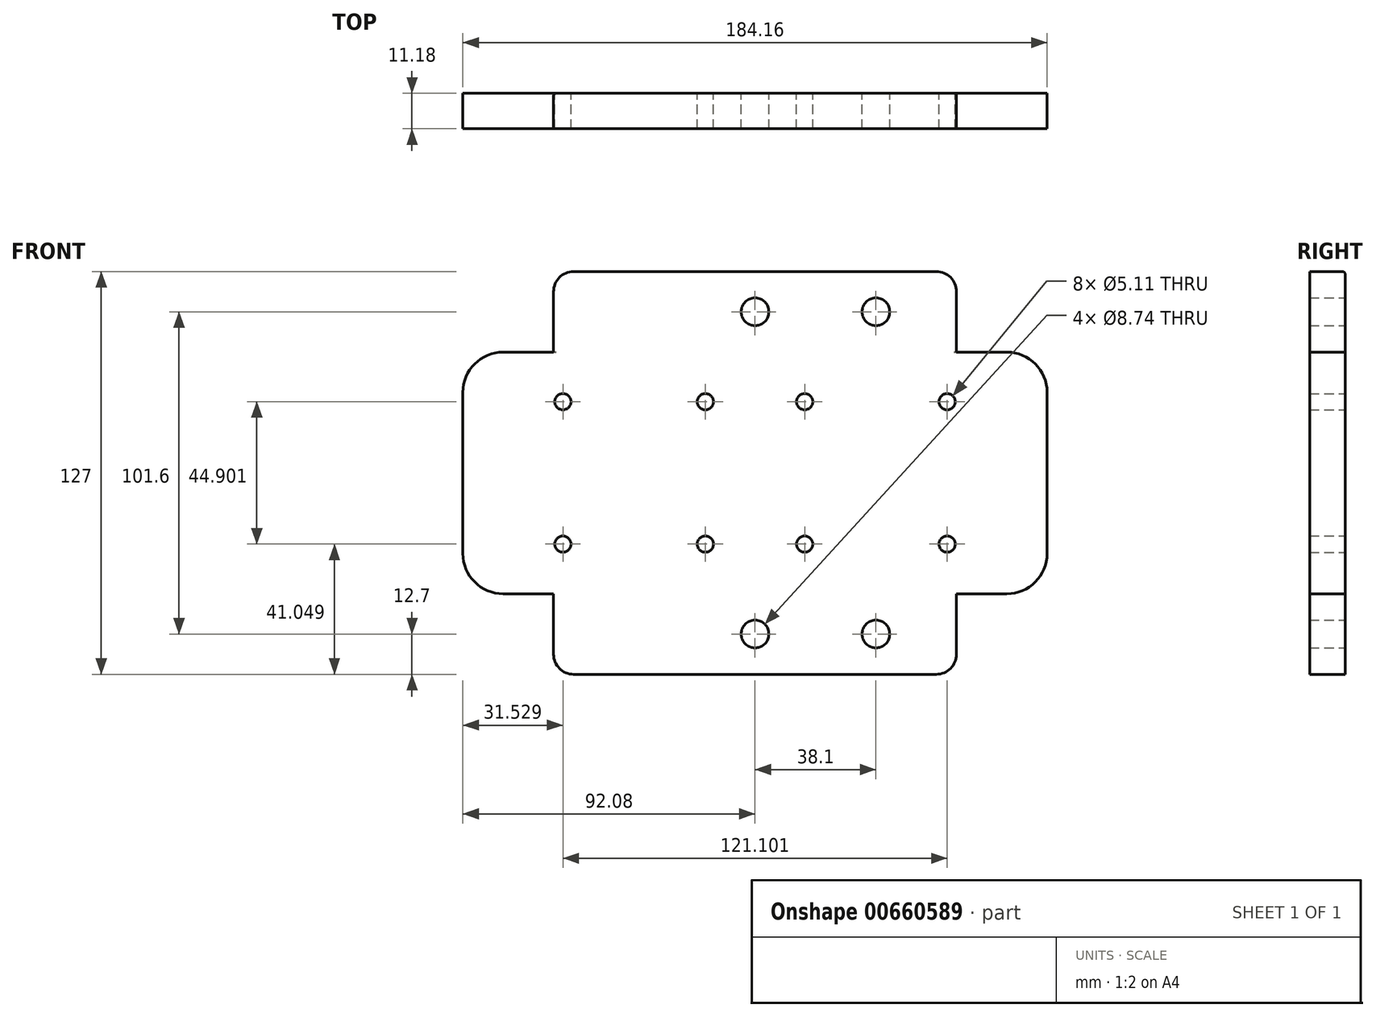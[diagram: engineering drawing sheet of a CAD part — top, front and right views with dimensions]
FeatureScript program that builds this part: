
annotation { "Feature Type Name" : "Feature", "Feature Type Description" : "" }
export const myFeature = defineFeature(function(context is Context, id is Id, definition is map)
    precondition{}
    {
        {
            var Q0;
            Q0=qCreatedBy(makeId("Front.planeOp"),FACE);
            var sketch = newSketch(context, id + "F0", { "sketchPlane" : qUnion([Q0])});
            skLineSegment(sketch, "E0.bottom", {"start": v(92.07, 38.1) * mm, "end": v(-92.08, 38.1) * mm});
            skLineSegment(sketch, "E0.top", {"start": v(92.08, -38.1) * mm, "end": v(-92.08, -38.1) * mm});
            skLineSegment(sketch, "E0.left", {"start": v(92.07, 38.1) * mm, "end": v(92.08, -38.1) * mm});
            skLineSegment(sketch, "E0.right", {"start": v(-92.08, 38.1) * mm, "end": v(-92.08, -38.1) * mm});
            skPoint(sketch, "E0.middle", {"position": v(0, 0) * mm});
            skPoint(sketch, "E1.visualSharp", {"position": v(-92.08, 38.1) * mm});
            skPoint(sketch, "E2.visualSharp", {"position": v(92.07, 38.1) * mm});
            skPoint(sketch, "E3.visualSharp", {"position": v(92.08, -38.1) * mm});
            skPoint(sketch, "E4.visualSharp", {"position": v(-92.08, -38.1) * mm});
            skSolve(sketch);
        }
        {
            var Q0;
            Q0 = qSketchRegion(id + "F0", true);
            extrude(context, id + "F1", {"entities" : qUnion([Q0]), "depth" : 11.18 * mm, "offsetDistance" : 25.4 * mm});
        }
        {
            var Q0;
            Q0=makeQuery(id+"F1.opExtrude","SWEPT_EDGE",EDGE,{"disambiguationData":[OSD([sQuery(id+"F0.wireOp",EDGE,"E0.bottom"),sQuery(id+"F0.wireOp",EDGE,"E0.left")])]});
            var Q1;
            Q1=makeQuery(id+"F1.opExtrude","SWEPT_EDGE",EDGE,{"disambiguationData":[OSD([sQuery(id+"F0.wireOp",EDGE,"E0.top"),sQuery(id+"F0.wireOp",EDGE,"E0.left")])]});
            var Q2;
            Q2=makeQuery(id+"F1.opExtrude","SWEPT_EDGE",EDGE,{"disambiguationData":[OSD([sQuery(id+"F0.wireOp",EDGE,"E0.top"),sQuery(id+"F0.wireOp",EDGE,"E0.right")])]});
            var Q3;
            Q3=makeQuery(id+"F1.opExtrude","SWEPT_EDGE",EDGE,{"disambiguationData":[OSD([sQuery(id+"F0.wireOp",EDGE,"E0.bottom"),sQuery(id+"F0.wireOp",EDGE,"E0.right")])]});
            fillet(context, id + "F2", {"entities" : qUnion([Q0, Q1, Q2, Q3]), "radius" : 12.7 * mm, "tangentPropagation" : true, "allowEdgeOverflow" : false});
        }
        {
            var Q0;
            Q0=qCreatedBy(makeId("Front.planeOp"),FACE);
            var sketch = newSketch(context, id + "F3", { "sketchPlane" : qUnion([Q0])});
            skLineSegment(sketch, "E5.bottom", {"start": v(63.5, 38.1) * mm, "end": v(-63.5, 38.1) * mm});
            skLineSegment(sketch, "E5.top", {"start": v(63.5, 63.5) * mm, "end": v(-63.5, 63.5) * mm});
            skLineSegment(sketch, "E5.left", {"start": v(63.5, 38.1) * mm, "end": v(63.5, 63.5) * mm});
            skLineSegment(sketch, "E5.right", {"start": v(-63.5, 38.1) * mm, "end": v(-63.5, 63.5) * mm});
            skLineSegment(sketch, "E6.MirrorCS", {"start": v(63.5, -38.1) * mm, "end": v(63.5, -63.5) * mm});
            skLineSegment(sketch, "E7.MirrorCS", {"start": v(63.5, -38.1) * mm, "end": v(-63.5, -38.1) * mm});
            skLineSegment(sketch, "E8.MirrorCS", {"start": v(63.5, -63.5) * mm, "end": v(-63.5, -63.5) * mm});
            skLineSegment(sketch, "E9.MirrorCS", {"start": v(-63.5, -38.1) * mm, "end": v(-63.5, -63.5) * mm});
            skSolve(sketch);
        }
        {
            var Q0;
            Q0 = qSketchRegion(id + "F3", true);
            var Q1;
            Q1=makeQuery(id+"F00pBhFej4blYbs_1.boolean.opBoolean","MERGE",FACE,{"derivedFrom":[makeQuery(id+"F1.opExtrude","CAP_FACE",FACE,{"disambiguationData":[OSD([sQuery(id+"F0.wireOp",EDGE,"E0.bottom"),sQuery(id+"F0.wireOp",EDGE,"E0.top"),sQuery(id+"F0.wireOp",EDGE,"E0.left"),sQuery(id+"F0.wireOp",EDGE,"E0.right")])],"isStart":false}),makeQuery(id+"F00pBhFej4blYbs_1.opExtrude","SWEPT_FACE",FACE,{"disambiguationData":[OSD([sQuery(id+"FrYmvnTRkbLSalc_1.wireOp",EDGE,"83ce238e-0b4e-4dba-95ea-3f2d73f66f50.0")])]})]});
            extrude(context, id + "F4", {"entities" : qUnion([Q0]), "operationType" : NewBodyOperationType.ADD, "depth" : 11.18 * mm, "endBoundEntityFace" : qUnion([Q1]), "offsetDistance" : 25.4 * mm});
        }
        {
            var Q0;
            Q0=makeQuery(id+"F4.opExtrude","SWEPT_EDGE",EDGE,{"disambiguationData":[OSD([sQuery(id+"F3.wireOp",EDGE,"E5.top"),sQuery(id+"F3.wireOp",EDGE,"E5.right")])]});
            var Q1;
            Q1=makeQuery(id+"F4.opExtrude","SWEPT_EDGE",EDGE,{"disambiguationData":[OSD([sQuery(id+"F3.wireOp",EDGE,"E5.bottom"),sQuery(id+"F3.wireOp",EDGE,"E5.right")])]});
            var Q2;
            Q2=makeQuery(id+"F4.opExtrude","SWEPT_EDGE",EDGE,{"disambiguationData":[OSD([sQuery(id+"F3.wireOp",EDGE,"E5.top"),sQuery(id+"F3.wireOp",EDGE,"E5.left")])]});
            var Q3;
            Q3=makeQuery(id+"F4.opExtrude","SWEPT_EDGE",EDGE,{"disambiguationData":[OSD([sQuery(id+"F3.wireOp",EDGE,"E5.bottom"),sQuery(id+"F3.wireOp",EDGE,"E5.left")])]});
            var Q4;
            Q4=makeQuery(id+"F4.opExtrude","SWEPT_EDGE",EDGE,{"disambiguationData":[OSD([sQuery(id+"F3.wireOp",EDGE,"bee59cae-cfc2-4cea-a917-d5b71f79a2c30.MirrorCS"),sQuery(id+"F3.wireOp",EDGE,"9766ef8f-4c6f-4ca8-8f5c-87a873976bbb0.MirrorCS")])]});
            var Q5;
            Q5=makeQuery(id+"F4.opExtrude","SWEPT_EDGE",EDGE,{"disambiguationData":[OSD([sQuery(id+"F3.wireOp",EDGE,"bee59cae-cfc2-4cea-a917-d5b71f79a2c30.MirrorCS"),sQuery(id+"F3.wireOp",EDGE,"e70125e1-1b46-4465-9598-3ad01c10a2c50.MirrorCS")])]});
            var Q6;
            Q6=makeQuery(id+"F4.opExtrude","SWEPT_EDGE",EDGE,{"disambiguationData":[OSD([sQuery(id+"F3.wireOp",EDGE,"e70125e1-1b46-4465-9598-3ad01c10a2c50.MirrorCS"),sQuery(id+"F3.wireOp",EDGE,"a5c8c08a-3a17-4db2-bac1-b567688d6f260.MirrorCS")])]});
            var Q7;
            Q7=makeQuery(id+"F4.opExtrude","SWEPT_EDGE",EDGE,{"disambiguationData":[OSD([sQuery(id+"F3.wireOp",EDGE,"a5c8c08a-3a17-4db2-bac1-b567688d6f260.MirrorCS"),sQuery(id+"F3.wireOp",EDGE,"9766ef8f-4c6f-4ca8-8f5c-87a873976bbb0.MirrorCS")])]});
            var Q8;
            Q8=makeQuery(id+"F4.opExtrude","SWEPT_EDGE",EDGE,{"disambiguationData":[OSD([sQuery(id+"F3.wireOp",EDGE,"E8.MirrorCS"),sQuery(id+"F3.wireOp",EDGE,"E9.MirrorCS")])]});
            var Q9;
            Q9=makeQuery(id+"F4.opExtrude","SWEPT_EDGE",EDGE,{"disambiguationData":[OSD([sQuery(id+"F3.wireOp",EDGE,"E6.MirrorCS"),sQuery(id+"F3.wireOp",EDGE,"E8.MirrorCS")])]});
            var Q10;
            Q10=makeQuery(id+"F4.opExtrude","SWEPT_EDGE",EDGE,{"disambiguationData":[OSD([sQuery(id+"F3.wireOp",EDGE,"E6.MirrorCS"),sQuery(id+"F3.wireOp",EDGE,"E7.MirrorCS")])]});
            var Q11;
            Q11=makeQuery(id+"F4.opExtrude","SWEPT_EDGE",EDGE,{"disambiguationData":[OSD([sQuery(id+"F3.wireOp",EDGE,"E7.MirrorCS"),sQuery(id+"F3.wireOp",EDGE,"E9.MirrorCS")])]});
            fillet(context, id + "F5", {"entities" : qUnion([Q0, Q1, Q2, Q3, Q4, Q5, Q6, Q7, Q8, Q9, Q10, Q11]), "radius" : 6.35 * mm, "tangentPropagation" : true, "allowEdgeOverflow" : false});
        }
        {
            var Q0;
            Q0=makeQuery(id+"F4.boolean.opBoolean","MERGE",FACE,{"derivedFrom":[makeQuery(id+"F00pBhFej4blYbs_1.boolean.opBoolean","MERGE",FACE,{"derivedFrom":[makeQuery(id+"F1.opExtrude","CAP_FACE",FACE,{"disambiguationData":[OSD([sQuery(id+"F0.wireOp",EDGE,"E0.bottom"),sQuery(id+"F0.wireOp",EDGE,"E0.top"),sQuery(id+"F0.wireOp",EDGE,"E0.left"),sQuery(id+"F0.wireOp",EDGE,"E0.right")])],"isStart":true}),makeQuery(id+"F00pBhFej4blYbs_1.opExtrude","SWEPT_FACE",FACE,{"disambiguationData":[OSD([sQuery(id+"FrYmvnTRkbLSalc_1.wireOp",EDGE,"e4dff771-9c85-4897-a216-aceb6e9e5d08.0")])]})]}),makeQuery(id+"F4.opExtrude","CAP_FACE",FACE,{"disambiguationData":[OSD([sQuery(id+"F3.wireOp",EDGE,"E5.bottom"),sQuery(id+"F3.wireOp",EDGE,"E5.top"),sQuery(id+"F3.wireOp",EDGE,"E5.left"),sQuery(id+"F3.wireOp",EDGE,"E5.right")])],"isStart":true})]});
            var sketch = newSketch(context, id + "F6", { "sketchPlane" : qUnion([Q0])});
            skPoint(sketch, "E10", {"position": v(-60.55, 22.45) * mm});
            skPoint(sketch, "E11", {"position": v(-15.65, -22.45) * mm});
            skPoint(sketch, "E12", {"position": v(-60.55, -22.45) * mm});
            skPoint(sketch, "E13", {"position": v(-15.65, 22.45) * mm});
            skPoint(sketch, "E14", {"position": v(15.65, 22.45) * mm});
            skPoint(sketch, "E15", {"position": v(15.65, -22.45) * mm});
            skPoint(sketch, "E16", {"position": v(60.55, -22.45) * mm});
            skPoint(sketch, "E17", {"position": v(60.55, 22.45) * mm});
            skLineSegment(sketch, "E18", {"start": v(-60.55, 22.45) * mm, "end": v(-15.65, -22.45) * mm, "construction": true});
            skLineSegment(sketch, "E19", {"start": v(15.65, 22.45) * mm, "end": v(60.55, -22.45) * mm, "construction": true});
            skLineSegment(sketch, "E20", {"start": v(60.55, 22.45) * mm, "end": v(15.65, -22.45) * mm, "construction": true});
            skLineSegment(sketch, "E21", {"start": v(-15.65, 22.45) * mm, "end": v(-60.55, -22.45) * mm, "construction": true});
            skPoint(sketch, "E22", {"position": v(-38.1, 0) * mm});
            skPoint(sketch, "E23", {"position": v(38.1, 0) * mm});
            skSolve(sketch);
        }
        {
            var Q0;
            Q0=sQuery(id+"F6.wireOp",VERTEX,"E10");
            var Q1;
            Q1=sQuery(id+"F6.wireOp",VERTEX,"E13");
            var Q2;
            Q2=sQuery(id+"F6.wireOp",VERTEX,"E12");
            var Q3;
            Q3=sQuery(id+"F6.wireOp",VERTEX,"E11");
            var Q4;
            Q4=sQuery(id+"F6.wireOp",VERTEX,"E14");
            var Q5;
            Q5=sQuery(id+"F6.wireOp",VERTEX,"E15");
            var Q6;
            Q6=sQuery(id+"F6.wireOp",VERTEX,"E17");
            var Q7;
            Q7=sQuery(id+"F6.wireOp",VERTEX,"E16");
            var Q8;
            Q8=makeQuery(id+"F1.opExtrude","SWEPT_BODY",BODY,{"disambiguationData":[OSD([sQuery(id+"F0.wireOp",EDGE,"E0.bottom"),sQuery(id+"F0.wireOp",EDGE,"E0.top"),sQuery(id+"F0.wireOp",EDGE,"E0.left"),sQuery(id+"F0.wireOp",EDGE,"E0.right")])]});
            hole(context, id + "F7", {"style" : HoleStyle.SIMPLE, "endStyle" : HoleEndStyle.THROUGH, "standardTappedOrClearance" : lookupTablePath({ "standard" : "ANSI", "engagement" : "75%", "pitch" : "20 tpi", "size" : "1/4", "type" : "Tapped" }), "standardBlindInLast" : lookupTablePath({ "standard" : "ANSI", "engagement" : "75%", "pitch" : "20 tpi", "size" : "1/4", "type" : "Tapped" }), "holeDiameter" : 5.1 * mm, "majorDiameter" : 6.35 * mm, "showTappedDepth" : true, "isTappedThrough" : true, "tappedDepth" : 12.7 * mm, "tapClearance" : 3, "startFromSketch" : true, "locations" : qUnion([Q0, Q1, Q2, Q3, Q4, Q5, Q6, Q7]), "scope" : qUnion([Q8])});
        }
        {
            var Q0;
            Q0=makeQuery(id+"F4.opExtrude","CAP_EDGE",EDGE,{"disambiguationData":[OSD([sQuery(id+"F3.wireOp",EDGE,"E5.top")])],"isStart":true});
            fillet(context, id + "F8", {"entities" : qUnion([Q0]), "radius" : 0.83 * mm, "tangentPropagation" : true, "allowEdgeOverflow" : false});
        }
        {
            var Q0;
            Q0=makeQuery(id+"F4.boolean.opBoolean","MERGE",FACE,{"derivedFrom":[makeQuery(id+"F00pBhFej4blYbs_1.boolean.opBoolean","MERGE",FACE,{"derivedFrom":[makeQuery(id+"F1.opExtrude","CAP_FACE",FACE,{"disambiguationData":[OSD([sQuery(id+"F0.wireOp",EDGE,"E0.bottom"),sQuery(id+"F0.wireOp",EDGE,"E0.top"),sQuery(id+"F0.wireOp",EDGE,"E0.left"),sQuery(id+"F0.wireOp",EDGE,"E0.right")])],"isStart":true}),makeQuery(id+"F00pBhFej4blYbs_1.opExtrude","SWEPT_FACE",FACE,{"disambiguationData":[OSD([sQuery(id+"FrYmvnTRkbLSalc_1.wireOp",EDGE,"e4dff771-9c85-4897-a216-aceb6e9e5d08.0")])]})]}),makeQuery(id+"F4.opExtrude","CAP_FACE",FACE,{"disambiguationData":[OSD([sQuery(id+"F3.wireOp",EDGE,"E5.bottom"),sQuery(id+"F3.wireOp",EDGE,"E5.top"),sQuery(id+"F3.wireOp",EDGE,"E5.left"),sQuery(id+"F3.wireOp",EDGE,"E5.right")])],"isStart":true})]});
            var sketch = newSketch(context, id + "F9", { "sketchPlane" : qUnion([Q0])});
            skPoint(sketch, "E24", {"position": v(-38.1, 50.8) * mm});
            skPoint(sketch, "E25", {"position": v(0, 50.8) * mm});
            skPoint(sketch, "E26", {"position": v(-38.1, -50.8) * mm});
            skPoint(sketch, "E27", {"position": v(0, -50.8) * mm});
            skSolve(sketch);
        }
        {
            var Q0;
            Q0=sQuery(id+"F9.wireOp",VERTEX,"E24");
            var Q1;
            Q1=sQuery(id+"F9.wireOp",VERTEX,"E25");
            var Q2;
            Q2=sQuery(id+"F9.wireOp",VERTEX,"E26");
            var Q3;
            Q3=sQuery(id+"F9.wireOp",VERTEX,"E27");
            var Q4;
            Q4=makeQuery(id+"F1.opExtrude","SWEPT_BODY",BODY,{"disambiguationData":[OSD([sQuery(id+"F0.wireOp",EDGE,"E0.bottom"),sQuery(id+"F0.wireOp",EDGE,"E0.top"),sQuery(id+"F0.wireOp",EDGE,"E0.left"),sQuery(id+"F0.wireOp",EDGE,"E0.right")])]});
            hole(context, id + "F10", {"style" : HoleStyle.SIMPLE, "endStyle" : HoleEndStyle.THROUGH, "standardTappedOrClearance" : lookupTablePath({ "fit" : "Normal (ASME)", "standard" : "ANSI", "size" : "5/16", "type" : "Clearance" }), "standardBlindInLast" : lookupTablePath({ "fit" : "Normal", "standard" : "ANSI", "size" : "5/16", "type" : "Clearance" }), "holeDiameter" : 8.74 * mm, "majorDiameter" : 6.35 * mm, "isTappedThrough" : true, "tappedDepth" : 12.7 * mm, "tapClearance" : 3, "startFromSketch" : true, "locations" : qUnion([Q0, Q1, Q2, Q3]), "scope" : qUnion([Q4])});
        }
    });
